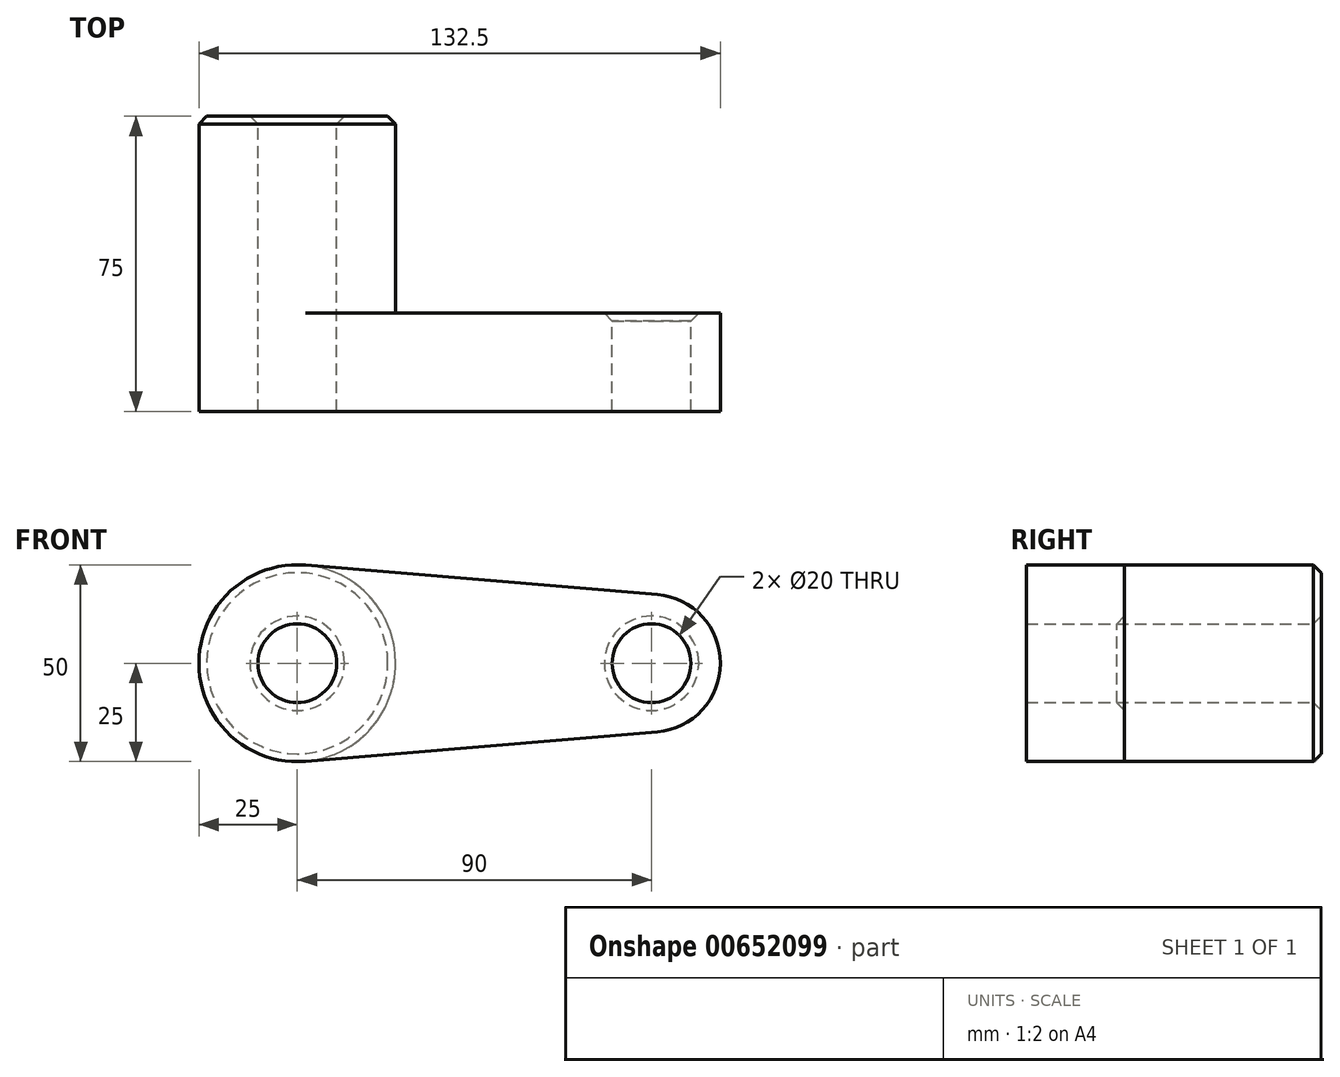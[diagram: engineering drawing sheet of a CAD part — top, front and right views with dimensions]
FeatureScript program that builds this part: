
annotation { "Feature Type Name" : "Feature", "Feature Type Description" : "" }
export const myFeature = defineFeature(function(context is Context, id is Id, definition is map)
    precondition{}
    {
        {
            var Q0;
            Q0=qCreatedBy(makeId("Front.planeOp"),FACE);
            var sketch = newSketch(context, id + "F0", { "sketchPlane" : qUnion([Q0])});
            skCircle(sketch, "E0", {"center": v(0, 0) * mm, "radius": 25 * mm});
            skCircle(sketch, "E1", {"center": v(90, 0) * mm, "radius": 17.5 * mm});
            skLineSegment(sketch, "E2", {"start": v(2.08, -24.91) * mm, "end": v(91.46, -17.44) * mm});
            skLineSegment(sketch, "E3", {"start": v(2.08, 24.91) * mm, "end": v(91.46, 17.44) * mm});
            skCircle(sketch, "E4", {"center": v(0, 0) * mm, "radius": 10 * mm});
            skCircle(sketch, "E5", {"center": v(90, 0) * mm, "radius": 10 * mm});
            skSolve(sketch);
        }
        {
            var Q0;
            Q0 = qSketchRegion(id + "F0", true);
            extrude(context, id + "F1", {"entities" : qUnion([Q0]), "depth" : 25 * mm, "offsetDistance" : 25.4 * mm});
        }
        {
            var Q0;
            Q0=makeQuery(id+"F0.imprint","IMPRINT",FACE,{"disambiguationData":[TD([[makeQuery(id+"F0.imprint","IMPRINT",EDGE,{"derivedFrom":sQuery(id+"F0.wireOp",EDGE,"E4")}),-1.0]])]});
            var Q1;
            Q1=sQuery(id+"F0.wireOp",EDGE,"E0");
            var Q2;
            Q2=sQuery(id+"F0.wireOp",EDGE,"E4");
            extrude(context, id + "F2", {"entities" : qUnion([Q0]), "operationType" : NewBodyOperationType.ADD, "surfaceEntities" : qUnion([Q1, Q2]), "oppositeDirection" : true, "depth" : 50 * mm, "offsetDistance" : 25.4 * mm});
        }
        {
            var Q0;
            Q0=makeQuery(id+"F2.opExtrude","CAP_EDGE",EDGE,{"disambiguationData":[OSD([sQuery(id+"F0.wireOp",EDGE,"E4")])],"isStart":false});
            var Q1;
            Q1=makeQuery(id+"F2.opExtrude","CAP_EDGE",EDGE,{"disambiguationData":[OSD([sQuery(id+"F0.wireOp",EDGE,"E0")])],"isStart":false});
            var Q2;
            Q2=makeQuery(id+"F1.opExtrude","CAP_EDGE",EDGE,{"disambiguationData":[OSD([sQuery(id+"F0.wireOp",EDGE,"E5")])],"isStart":true});
            chamfer(context, id + "F3", {"entities" : qUnion([Q0, Q1, Q2]), "width" : 2 * mm, "tangentPropagation" : true});
        }
    });
